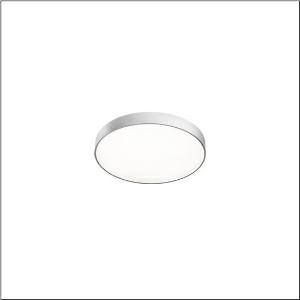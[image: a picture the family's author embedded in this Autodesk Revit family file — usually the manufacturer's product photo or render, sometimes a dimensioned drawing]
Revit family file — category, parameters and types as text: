
# Revit family: round_21_s_51mr34fd0421s
name_source: partatom
category: Lighting Fixtures
units: mm (PartAtom-declared; Revit-internal decimal feet)

## family parameters
Cut with Voids When Loaded = No
Host = Face
Light Source = No
Part Type = Normal
Room Calculation Point = No
Round Connector Dimension = Use Diameter
Shared = No

## types (1)
- Round 21 S (1 x LED, 3910 lm, 30.3 W, 4000K)
    Apparent Load = 30 VA
    CIE Flux Codes = 49 80 96 100 100
    Color Rendering = 80
    Color Temperature = 4000K
    Default Elevation = 1800 mm
    Description = Round 21 S, wall and ceiling luminaire, primary optical cover: cover, of PMMA, opal, light emission: direct distribution, primary light characteristic: symmetric, installation type: suspended mounting, surface-mounted, LED, rated luminous flux: 3.900lm, luminous efficacy: 129lm/W, light colour: 840, colour temperature: 4000K, control gear: DALI 2, with terminal, 5-pole, mains connection: 230V, AC, 50/60Hz, rated input power: 30.3W, housing, of aluminium, coated, silver, diameter: 400mm, height: 62mm, protection rating (complete): IP40, insulation class (complete): insulation class I (protective earthing), certification: CE, impact resistance: IK04, permissible operating ambient temperature: -10..+35°C, packaging unit: 1 piece
    Height = 87 mm
    Lamp = 1 x LED
    Lamp Light Flux = 3910 lm
    Lamp Power = 30.3 W
    Lamp count = 1
    Length = 400 mm
    Luminous efficacy = 129 lm/W
    Manufacturer = Siteco
    ModVariant = No
    Model = 51MR34FD0421S
    Mounting Place = Wall
    Mounting Type = Surface mounted
    Number of Poles = 1
    OnlyDefault = Yes
    Power Factor = 1
    Product Name = Round 21 S
    Product group = wall and ceiling luminaire
    ProductGroupID = 2001
    Protection Class = Protection class I
    Protection Degree = IP 40
    RLX_Detail_Level = 1
    RLX_Emergency_Light_Flux = 0 lm
    RLX_Emergency_Type = 0
    RLX_Emergency_Type_DB = No
    RlxData = <blob elided: 11141 chars, md5=70677c38>
    Socket = socket
    Standby Power = 0 W
    System Light Flux = 3910 lm
    System Power = 30 W
    Type Comments = Product without accessories
    Type Image = l_1258309.jpg
    URL = http://relux.com
    VarID = ---
    Voltage = 0 V
    Weight = 0.00 kg
    Width = 0 mm  [stored 0 ft]

note: [stored X ft] marks values corroborated as IEEE doubles in the binary element streams (Revit-internal decimal feet)

## geometry (parser evidence)
native form markers: Sweep x8
no freeform markers — native parametric forms only
